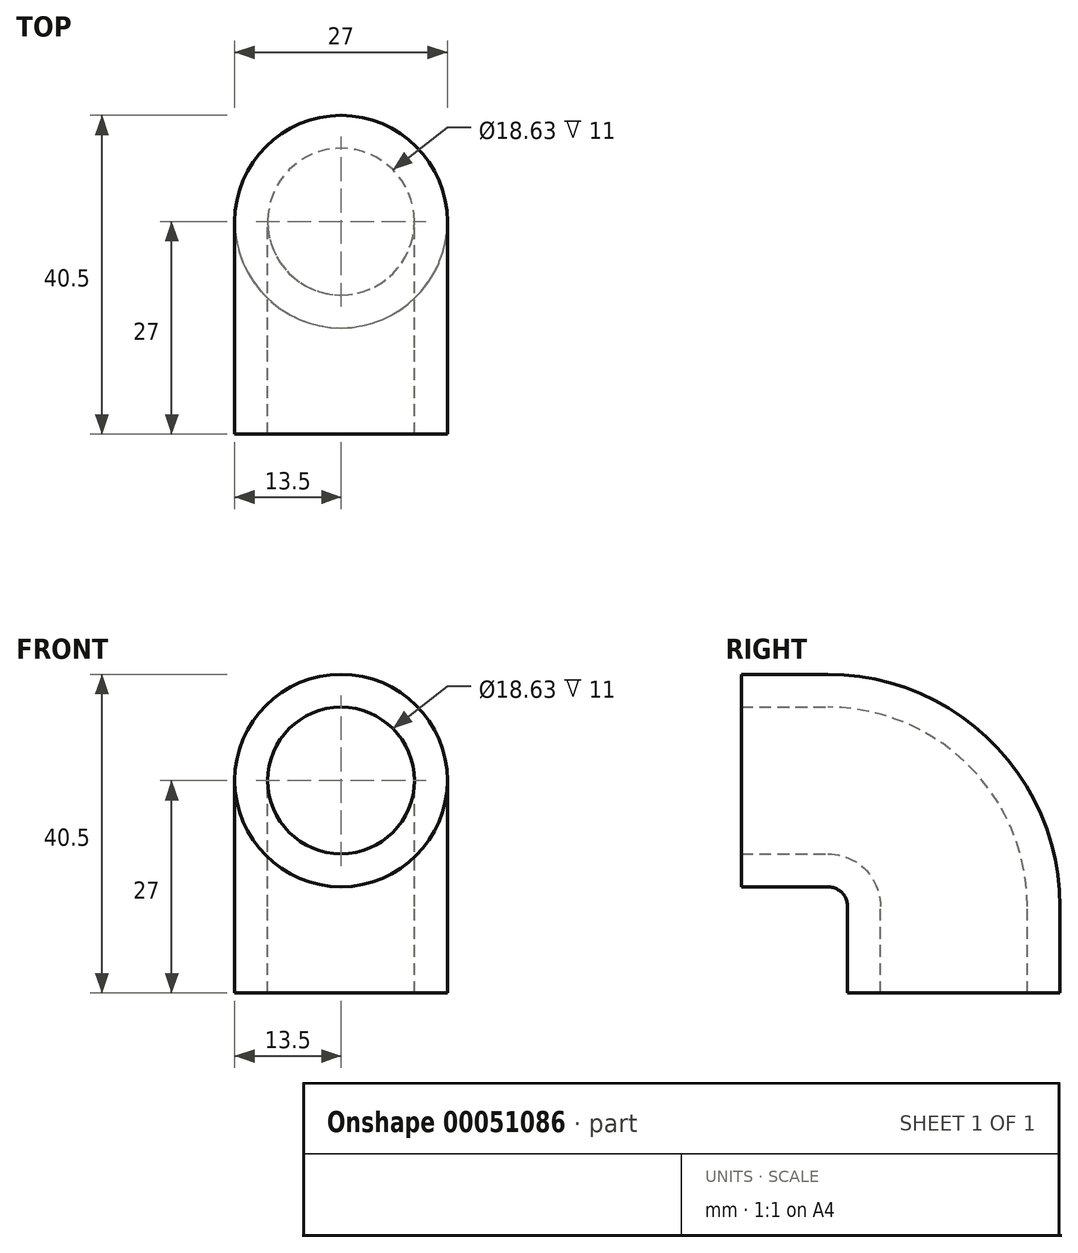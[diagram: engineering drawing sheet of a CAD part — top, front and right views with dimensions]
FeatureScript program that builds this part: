
annotation { "Feature Type Name" : "Feature", "Feature Type Description" : "" }
export const myFeature = defineFeature(function(context is Context, id is Id, definition is map)
    precondition{}
    {
        {
            var Q0;
            Q0=qCreatedBy(makeId("Front.planeOp"),FACE);
            var sketch = newSketch(context, id + "F0", { "sketchPlane" : qUnion([Q0])});
            skCircle(sketch, "E0", {"center": v(0, 0) * mm, "radius": 9.32 * mm});
            skCircle(sketch, "E1", {"center": v(0, 0) * mm, "radius": 13.5 * mm});
            skSolve(sketch);
        }
        {
            var Q0;
            Q0=qSketchRegion(id+"F0",true);
            extrude(context, id + "F1", {"entities" : qUnion([Q0]), "depth" : 11 * mm});
        }
        {
            var Q0;
            Q0=qCreatedBy(makeId("Right.planeOp"),FACE);
            var sketch = newSketch(context, id + "F2", { "sketchPlane" : qUnion([Q0])});
            skLineSegment(sketch, "E2", {"start": v(-3.28, -16) * mm, "end": v(26.95, -16) * mm});
            skArc(sketch, "E3", {"start": v(0, 0) * mm, "mid": v(11.31, -4.69) * mm, "end": v(16, -16) * mm});
            skSolve(sketch);
        }
        {
            var Q0;
            Q0=makeQuery(id+"F1.opExtrude","CAP_FACE",FACE,{"disambiguationData":[OSD([sQuery(id+"F0.wireOp",EDGE,"E0"),sQuery(id+"F0.wireOp",EDGE,"E1")])],"isStart":true});
            var Q1;
            Q1=sQuery(id+"F2.wireOp",EDGE,"E3");
            sweep(context, id + "F3", {"operationType" : NewBodyOperationType.ADD, "profiles" : qUnion([Q0]), "path" : qUnion([Q1])});
        }
        {
            var Q0;
            Q0=makeQuery(id+"F3.opSweep","CAP_FACE",FACE,{"disambiguationData":[OSD([sQuery(id+"F0.wireOp",EDGE,"E0"),sQuery(id+"F0.wireOp",EDGE,"E1"),sQuery(id+"F2.wireOp",VERTEX,"E3.end")])],"isStart":false});
            var sketch = newSketch(context, id + "F4", { "sketchPlane" : qUnion([Q0])});
            skCircle(sketch, "E4", {"center": v(0, -16) * mm, "radius": 9.32 * mm});
            skCircle(sketch, "E5", {"center": v(0, -16) * mm, "radius": 13.5 * mm});
            skSolve(sketch);
        }
        {
            var Q0;
            Q0=qSketchRegion(id+"F4",true);
            extrude(context, id + "F5", {"entities" : qUnion([Q0]), "operationType" : NewBodyOperationType.ADD, "depth" : 11 * mm});
        }
    });
